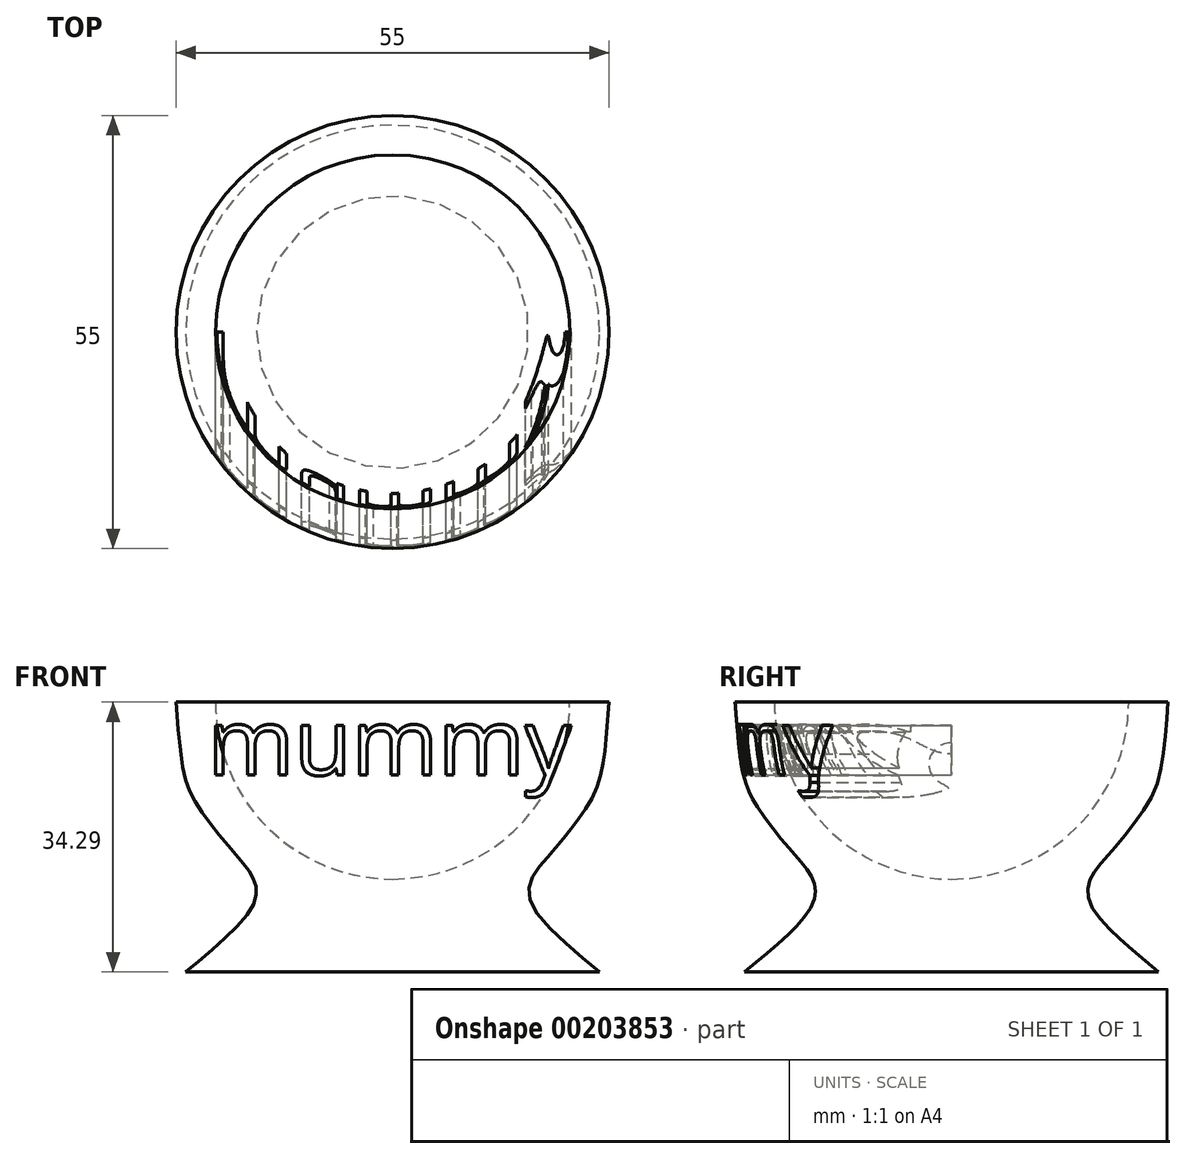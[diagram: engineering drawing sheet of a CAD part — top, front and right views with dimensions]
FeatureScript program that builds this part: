
annotation { "Feature Type Name" : "Feature", "Feature Type Description" : "" }
export const myFeature = defineFeature(function(context is Context, id is Id, definition is map)
    precondition{}
    {
        {
            var Q0;
            Q0=qCreatedBy(makeId("Front.planeOp"),FACE);
            var sketch = newSketch(context, id + "F0", { "sketchPlane" : qUnion([Q0])});
            skLineSegment(sketch, "E0", {"start": v(0, 0) * mm, "end": v(0, 34.29) * mm});
            skLineSegment(sketch, "E1", {"start": v(0, 0) * mm, "end": v(-26.28, 0) * mm});
            skCircle(sketch, "E2", {"center": v(0, 34.29) * mm, "radius": 22.5 * mm});
            skLineSegment(sketch, "E3", {"start": v(-22.5, 34.29) * mm, "end": v(-27.5, 34.29) * mm});
            skFitSpline(sketch, "E4", {"points": [v(-27.5, 34.29) * mm, v(-25.12, 21.75) * mm, v(-20.18, 15.17) * mm, v(-17.64, 11.78) * mm, v(-17.86, 8.17) * mm, v(-26.28, 0) * mm], "startDerivative": vector(6.98, -90.7) * mm, "endDerivative": vector(-34.85, -30.01) * mm});
            skSolve(sketch);
        }
        {
            var Q0;
            {var subQ4=sQuery(id+"F0.wireOp",EDGE,"E1");Q0=makeQuery(id+"F0.imprint","IMPRINT",FACE,{"disambiguationData":[TD([[makeQuery(id+"F0.imprint","IMPRINT",EDGE,{"derivedFrom":subQ4}),-1.0]])]});}
            var Q1;
            Q1=sQuery(id+"F0.wireOp",EDGE,"E0");
            revolve(context, id + "F1", {"entities" : qUnion([Q0]), "axis" : qUnion([Q1]), "revolveType" : RevolveType.FULL});
        }
        {
            var Q0;
            Q0=qCreatedBy(makeId("Front.planeOp"),FACE);
            var sketch = newSketch(context, id + "F2", { "sketchPlane" : qUnion([Q0])});
            skText(sketch, "E5", { "text": "mummy", "fontName": "OpenSans-Regular.ttf"});
            skLineSegment(sketch, "E6", {"start": v(0, 25) * mm, "end": v(0, 0) * mm});
            const initialGuessF2  = {"E5": [-0.0235, 0.025, 1, 0, 0.00852]};
            skSetInitialGuess(sketch, initialGuessF2);
            skSolve(sketch);
        }
        {
            var Q0;
            Q0 = qSketchRegion(id + "F2", true);
            extrude(context, id + "F3", {"entities" : qUnion([Q0]), "operationType" : NewBodyOperationType.REMOVE, "depth" : 50.5 * mm});
        }
    });
